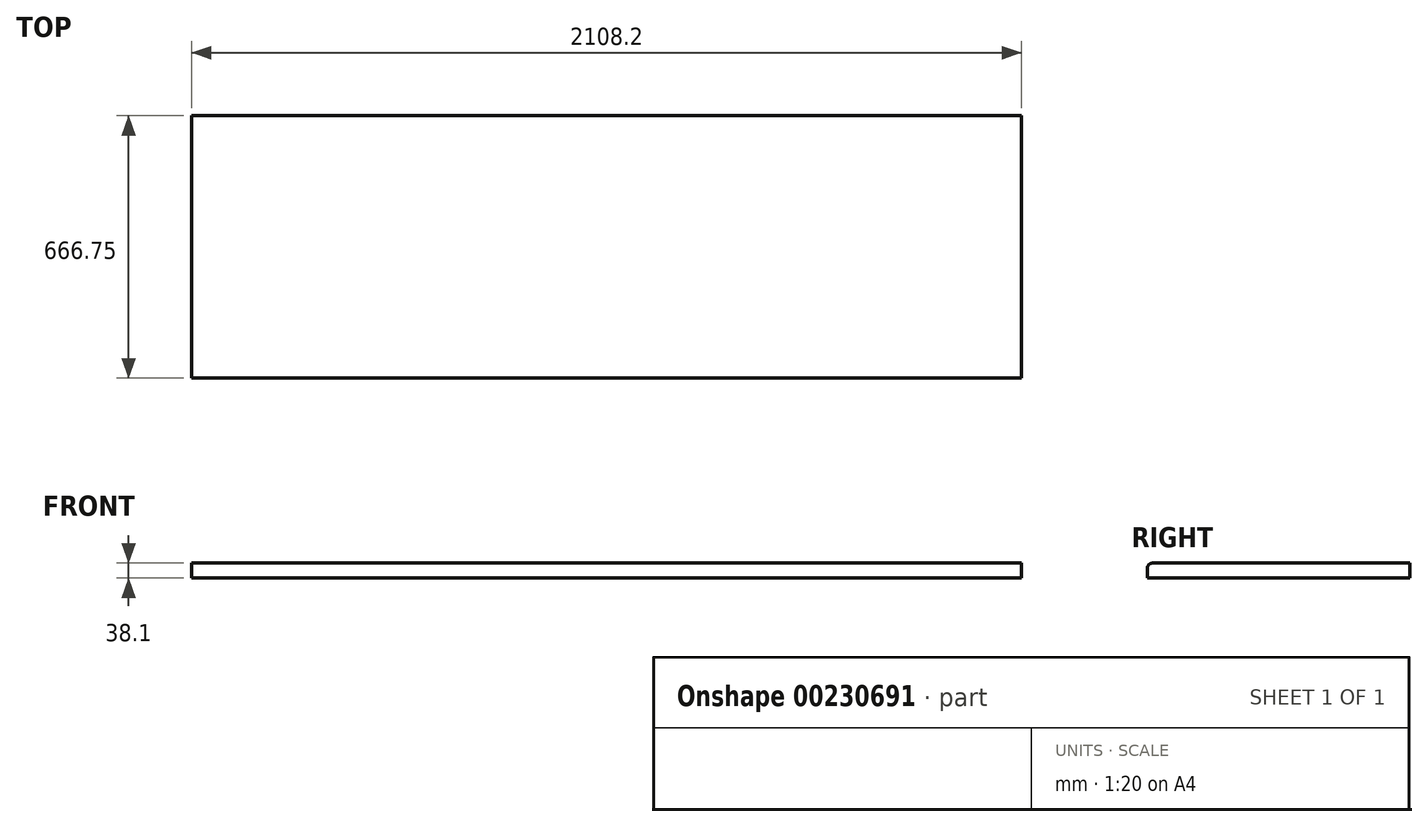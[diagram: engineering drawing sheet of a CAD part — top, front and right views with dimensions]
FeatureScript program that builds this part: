
annotation { "Feature Type Name" : "Feature", "Feature Type Description" : "" }
export const myFeature = defineFeature(function(context is Context, id is Id, definition is map)
    precondition{}
    {
        {
            var Q0;
            Q0=qCreatedBy(makeId("Front.planeOp"),FACE);
            var sketch = newSketch(context, id + "F0", { "sketchPlane" : qUnion([Q0])});
            skLineSegment(sketch, "E0.bottom", {"start": v(-52.62, 17.12) * mm, "end": v(2055.58, 17.12) * mm});
            skLineSegment(sketch, "E0.top", {"start": v(-52.62, -20.98) * mm, "end": v(2055.58, -20.98) * mm});
            skLineSegment(sketch, "E0.left", {"start": v(-52.62, 17.12) * mm, "end": v(-52.62, -20.98) * mm});
            skLineSegment(sketch, "E0.right", {"start": v(2055.58, 17.12) * mm, "end": v(2055.58, -20.98) * mm});
            skSolve(sketch);
        }
        {
            var Q0;
            Q0=makeQuery(id+"F0.imprint","IMPRINT",FACE,{"disambiguationData":[TD([[makeQuery(id+"F0.imprint","IMPRINT",EDGE,{"derivedFrom":sQuery(id+"F0.wireOp",EDGE,"E0.bottom")}),-1.0]])]});
            extrude(context, id + "F1", {"entities" : qUnion([Q0]), "oppositeDirection" : true, "depth" : 666.75 * mm});
        }
        {
            var Q0;
            Q0=makeQuery(id+"F1.opExtrude","CAP_EDGE",EDGE,{"disambiguationData":[OSD([sQuery(id+"F0.wireOp",EDGE,"E0.bottom")])],"isStart":true});
            fillet(context, id + "F2", {"entities" : qUnion([Q0]), "radius" : 12.7 * mm, "tangentPropagation" : true, "allowEdgeOverflow" : false});
        }
    });
